FCSTD DOCUMENT  (FreeCAD 0.19R24291 (Git))
Label: test
License: All rights reserved
LicenseURL: http://en.wikipedia.org/wiki/All_rights_reserved
objects: Part::Part2DObjectPython×59
note: 59 computed .brp shape members not serialized (recipe doc carries the construction recipe); baked Part::Feature solids carry a one-line shape summary decoded from their .brp

FEATURE [Part::Part2DObjectPython] Line  # Draft 2D object (typed FeaturePython)
  Area = 0
  ChamferSize = 0
  Closed = false
  End = (-1266.79,1133.62,0)
  FilletRadius = 0
  Length = 3029.77
  MakeFace = true
  Points = (2) [(-901.491,-1874.05,0),(-1266.79,1133.62,0)]
  Start = (-901.491,-1874.05,0)
  Subdivisions = 0
  type = Beam
FEATURE [Part::Part2DObjectPython] Line001  # Draft 2D object (typed FeaturePython)
  Area = 0
  ChamferSize = 0
  Closed = false
  End = (-719.583,3387.59,0)
  FilletRadius = 0
  Length = 2319.45
  MakeFace = true
  Points = (2) [(-1266.79,1133.62,0),(-719.583,3387.59,0)]
  Start = (-1266.79,1133.62,0)
  Subdivisions = 0
  type = Beam
FEATURE [Part::Part2DObjectPython] Line002  # Draft 2D object (typed FeaturePython)
  Area = 0
  ChamferSize = 0
  Closed = false
  End = (-585.639,4946.22,0)
  FilletRadius = 0
  Length = 1564.37
  MakeFace = true
  Points = (2) [(-719.583,3387.59,0),(-585.639,4946.22,0)]
  Start = (-719.583,3387.59,0)
  Subdivisions = 0
  type = Beam
FEATURE [Part::Part2DObjectPython] Line003  # Draft 2D object (typed FeaturePython)
  Area = 0
  ChamferSize = 0
  Closed = false
  End = (-208.337,6520.16,0)
  FilletRadius = 0
  Length = 1618.53
  MakeFace = true
  Points = (2) [(-585.639,4946.22,0),(-208.337,6520.16,0)]
  Start = (-585.639,4946.22,0)
  Subdivisions = 0
  type = Beam
FEATURE [Part::Part2DObjectPython] Line004  # Draft 2D object (typed FeaturePython)
  Area = 0
  ChamferSize = 0
  Closed = false
  End = (510.393,7946.01,0)
  FilletRadius = 0
  Length = 1596.75
  MakeFace = true
  Points = (2) [(-208.337,6520.16,0),(510.393,7946.01,0)]
  Start = (-208.337,6520.16,0)
  Subdivisions = 0
  type = Beam
FEATURE [Part::Part2DObjectPython] Line005  # Draft 2D object (typed FeaturePython)
  Area = 0
  ChamferSize = 0
  Closed = false
  End = (486.04,9054.09,0)
  FilletRadius = 0
  Length = 1108.35
  MakeFace = true
  Points = (2) [(510.393,7946.01,0),(486.04,9054.09,0)]
  Start = (510.393,7946.01,0)
  Subdivisions = 0
  type = Beam
FEATURE [Part::Part2DObjectPython] Line006  # Draft 2D object (typed FeaturePython)
  Area = 0
  ChamferSize = 0
  Closed = false
  End = (120.663,10554.8,0)
  FilletRadius = 0
  Length = 1544.54
  MakeFace = true
  Points = (2) [(486.04,9054.09,0),(120.663,10554.8,0)]
  Start = (486.04,9054.09,0)
  Subdivisions = 0
  type = Beam
FEATURE [Part::Part2DObjectPython] Line007  # Draft 2D object (typed FeaturePython)
  Area = 0
  ChamferSize = 0
  Closed = false
  End = (-2616.71,977.139,0)
  FilletRadius = 0
  Length = 2215.24
  MakeFace = true
  Points = (2) [(-4757.6,408.041,0),(-2616.71,977.139,0)]
  Start = (-4757.6,408.041,0)
  Subdivisions = 0
  type = Beam
FEATURE [Part::Part2DObjectPython] Line008  # Draft 2D object (typed FeaturePython)
  Area = 0
  ChamferSize = 0
  Closed = false
  End = (-1912.11,841.639,0)
  FilletRadius = 0
  Length = 717.507
  MakeFace = true
  Points = (2) [(-2616.71,977.139,0),(-1912.11,841.639,0)]
  Start = (-2616.71,977.139,0)
  Subdivisions = 0
  type = Beam
FEATURE [Part::Part2DObjectPython] Line009  # Draft 2D object (typed FeaturePython)
  Area = 0
  ChamferSize = 0
  Closed = false
  End = (-1266.79,1133.62,0)
  FilletRadius = 0
  Length = 708.299
  MakeFace = true
  Points = (2) [(-1912.11,841.639,0),(-1266.79,1133.62,0)]
  Start = (-1912.11,841.639,0)
  Subdivisions = 0
  type = Beam
FEATURE [Part::Part2DObjectPython] Line010  # Draft 2D object (typed FeaturePython)
  Area = 0
  ChamferSize = 0
  Closed = false
  End = (-150.615,977.139,0)
  FilletRadius = 0
  Length = 1127.09
  MakeFace = true
  Points = (2) [(-1266.79,1133.62,0),(-150.615,977.139,0)]
  Start = (-1266.79,1133.62,0)
  Subdivisions = 0
  type = Beam
FEATURE [Part::Part2DObjectPython] Line011  # Draft 2D object (typed FeaturePython)
  Area = 0
  ChamferSize = 0
  Closed = false
  End = (716.583,706.14,0)
  FilletRadius = 0
  Length = 908.555
  MakeFace = true
  Points = (2) [(-150.615,977.139,0),(716.583,706.14,0)]
  Start = (-150.615,977.139,0)
  Subdivisions = 0
  type = Beam
FEATURE [Part::Part2DObjectPython] Line012  # Draft 2D object (typed FeaturePython)
  Area = 0
  ChamferSize = 0
  Closed = false
  End = (1583.78,733.239,0)
  FilletRadius = 0
  Length = 867.621
  MakeFace = true
  Points = (2) [(716.583,706.14,0),(1583.78,733.239,0)]
  Start = (716.583,706.14,0)
  Subdivisions = 0
  type = Beam
FEATURE [Part::Part2DObjectPython] Line013  # Draft 2D object (typed FeaturePython)
  Area = 0
  ChamferSize = 0
  Closed = false
  End = (2559.38,977.139,0)
  FilletRadius = 0
  Length = 1005.62
  MakeFace = true
  Points = (2) [(1583.78,733.239,0),(2559.38,977.139,0)]
  Start = (1583.78,733.239,0)
  Subdivisions = 0
  type = Beam
FEATURE [Part::Part2DObjectPython] Line014  # Draft 2D object (typed FeaturePython)
  Area = 0
  ChamferSize = 0
  Closed = false
  End = (3372.38,1329.44,0)
  FilletRadius = 0
  Length = 886.048
  MakeFace = true
  Points = (2) [(2559.38,977.139,0),(3372.38,1329.44,0)]
  Start = (2559.38,977.139,0)
  Subdivisions = 0
  type = Beam
FEATURE [Part::Part2DObjectPython] Line015  # Draft 2D object (typed FeaturePython)
  Area = 0
  ChamferSize = 0
  Closed = false
  End = (4185.37,1546.24,0)
  FilletRadius = 0
  Length = 841.407
  MakeFace = true
  Points = (2) [(3372.38,1329.44,0),(4185.37,1546.24,0)]
  Start = (3372.38,1329.44,0)
  Subdivisions = 0
  type = Beam
FEATURE [Part::Part2DObjectPython] Line016  # Draft 2D object (typed FeaturePython)
  Area = 0
  ChamferSize = 0
  Closed = false
  End = (5079.67,1356.54,0)
  FilletRadius = 0
  Length = 914.196
  MakeFace = true
  Points = (2) [(4185.37,1546.24,0),(5079.67,1356.54,0)]
  Start = (4185.37,1546.24,0)
  Subdivisions = 0
  type = Beam
FEATURE [Part::Part2DObjectPython] Line017  # Draft 2D object (typed FeaturePython)
  Area = 0
  ChamferSize = 0
  Closed = false
  End = (-1017.81,9351.02,0)
  FilletRadius = 0
  Length = 1656.87
  MakeFace = true
  Points = (2) [(120.663,10554.8,0),(-1017.81,9351.02,0)]
  Start = (120.663,10554.8,0)
  Subdivisions = 0
  type = Beam
FEATURE [Part::Part2DObjectPython] Line018  # Draft 2D object (typed FeaturePython)
  Area = 0
  ChamferSize = 0
  Closed = false
  End = (-2481.21,8971.62,0)
  FilletRadius = 0
  Length = 1511.78
  MakeFace = true
  Points = (2) [(-1017.81,9351.02,0),(-2481.21,8971.62,0)]
  Start = (-1017.81,9351.02,0)
  Subdivisions = 0
  type = Beam
FEATURE [Part::Part2DObjectPython] Line019  # Draft 2D object (typed FeaturePython)
  Area = 0
  ChamferSize = 0
  Closed = false
  End = (-3656.96,8788.47,0)
  FilletRadius = 0
  Length = 1189.93
  MakeFace = true
  Points = (2) [(-2481.21,8971.62,0),(-3656.96,8788.47,0)]
  Start = (-2481.21,8971.62,0)
  Subdivisions = 0
  type = Beam
FEATURE [Part::Part2DObjectPython] Line020  # Draft 2D object (typed FeaturePython)
  Area = 0
  ChamferSize = 0
  Closed = false
  End = (-4567.9,8131.52,0)
  FilletRadius = 0
  Length = 1123.12
  MakeFace = true
  Points = (2) [(-3656.96,8788.47,0),(-4567.9,8131.52,0)]
  Start = (-3656.96,8788.47,0)
  Subdivisions = 0
  type = Beam
FEATURE [Part::Part2DObjectPython] Line021  # Draft 2D object (typed FeaturePython)
  Area = 0
  ChamferSize = 0
  Closed = false
  End = (-5868.7,7101.72,0)
  FilletRadius = 0
  Length = 1659.08
  MakeFace = true
  Points = (2) [(-4567.9,8131.52,0),(-5868.7,7101.72,0)]
  Start = (-4567.9,8131.52,0)
  Subdivisions = 0
  type = Beam
FEATURE [Part::Part2DObjectPython] Line022  # Draft 2D object (typed FeaturePython)
  Area = 0
  ChamferSize = 0
  Closed = false
  End = (-6112.6,5936.43,0)
  FilletRadius = 0
  Length = 1190.55
  MakeFace = true
  Points = (2) [(-5868.7,7101.72,0),(-6112.6,5936.43,0)]
  Start = (-5868.7,7101.72,0)
  Subdivisions = 0
  type = Beam
FEATURE [Part::Part2DObjectPython] Line023  # Draft 2D object (typed FeaturePython)
  Area = 0
  ChamferSize = 0
  Closed = false
  End = (-6790.1,4852.43,0)
  FilletRadius = 0
  Length = 1278.3
  MakeFace = true
  Points = (2) [(-6112.6,5936.43,0),(-6790.1,4852.43,0)]
  Start = (-6112.6,5936.43,0)
  Subdivisions = 0
  type = Beam
FEATURE [Part::Part2DObjectPython] Line024  # Draft 2D object (typed FeaturePython)
  Area = 0
  ChamferSize = 0
  Closed = false
  End = (-6817.2,3903.93,0)
  FilletRadius = 0
  Length = 948.886
  MakeFace = true
  Points = (2) [(-6790.1,4852.43,0),(-6817.2,3903.93,0)]
  Start = (-6790.1,4852.43,0)
  Subdivisions = 0
  type = Beam
FEATURE [Part::Part2DObjectPython] Line025  # Draft 2D object (typed FeaturePython)
  Area = 0
  ChamferSize = 0
  Closed = false
  End = (-6519.1,2955.43,0)
  FilletRadius = 0
  Length = 994.239
  MakeFace = true
  Points = (2) [(-6817.2,3903.93,0),(-6519.1,2955.43,0)]
  Start = (-6817.2,3903.93,0)
  Subdivisions = 0
  type = Beam
FEATURE [Part::Part2DObjectPython] Line026  # Draft 2D object (typed FeaturePython)
  Area = 0
  ChamferSize = 0
  Closed = false
  End = (-5977.1,1871.44,0)
  FilletRadius = 0
  Length = 1211.95
  MakeFace = true
  Points = (2) [(-6519.1,2955.43,0),(-5977.1,1871.44,0)]
  Start = (-6519.1,2955.43,0)
  Subdivisions = 0
  type = Beam
FEATURE [Part::Part2DObjectPython] Line027  # Draft 2D object (typed FeaturePython)
  Area = 0
  ChamferSize = 0
  Closed = false
  End = (-4757.6,408.041,0)
  FilletRadius = 0
  Length = 1904.91
  MakeFace = true
  Points = (2) [(-5977.1,1871.44,0),(-4757.6,408.041,0)]
  Start = (-5977.1,1871.44,0)
  Subdivisions = 0
  type = Beam
FEATURE [Part::Part2DObjectPython] Line028  # Draft 2D object (typed FeaturePython)
  Area = 0
  ChamferSize = 0
  Closed = false
  End = (1126.94,11916.2,0)
  FilletRadius = 0
  Length = 1692.96
  MakeFace = true
  Points = (2) [(120.663,10554.8,0),(1126.94,11916.2,0)]
  Start = (120.663,10554.8,0)
  Subdivisions = 0
  type = Beam
FEATURE [Part::Part2DObjectPython] Line029  # Draft 2D object (typed FeaturePython)
  Area = 0
  ChamferSize = 0
  Closed = false
  End = (2347.26,12515.3,0)
  FilletRadius = 0
  Length = 1359.43
  MakeFace = true
  Points = (2) [(1126.94,11916.2,0),(2347.26,12515.3,0)]
  Start = (1126.94,11916.2,0)
  Subdivisions = 0
  type = Beam
FEATURE [Part::Part2DObjectPython] Line030  # Draft 2D object (typed FeaturePython)
  Area = 0
  ChamferSize = 0
  Closed = false
  End = (3745.07,12914.7,0)
  FilletRadius = 0
  Length = 1453.75
  MakeFace = true
  Points = (2) [(2347.26,12515.3,0),(3745.07,12914.7,0)]
  Start = (2347.26,12515.3,0)
  Subdivisions = 0
  type = Beam
FEATURE [Part::Part2DObjectPython] Line031  # Draft 2D object (typed FeaturePython)
  Area = 0
  ChamferSize = 0
  Closed = false
  End = (5231.64,12892.5,0)
  FilletRadius = 0
  Length = 1486.73
  MakeFace = true
  Points = (2) [(3745.07,12914.7,0),(5231.64,12892.5,0)]
  Start = (3745.07,12914.7,0)
  Subdivisions = 0
  type = Beam
FEATURE [Part::Part2DObjectPython] Line032  # Draft 2D object (typed FeaturePython)
  Area = 0
  ChamferSize = 0
  Closed = false
  End = (6474.14,12404.4,0)
  FilletRadius = 0
  Length = 1334.95
  MakeFace = true
  Points = (2) [(5231.64,12892.5,0),(6474.14,12404.4,0)]
  Start = (5231.64,12892.5,0)
  Subdivisions = 0
  type = Beam
FEATURE [Part::Part2DObjectPython] Line033  # Draft 2D object (typed FeaturePython)
  Area = 0
  ChamferSize = 0
  Closed = false
  End = (7295.08,11716.5,0)
  FilletRadius = 0
  Length = 1070.99
  MakeFace = true
  Points = (2) [(6474.14,12404.4,0),(7295.08,11716.5,0)]
  Start = (6474.14,12404.4,0)
  Subdivisions = 0
  type = Beam
FEATURE [Part::Part2DObjectPython] Line034  # Draft 2D object (typed FeaturePython)
  Area = 0
  ChamferSize = 0
  Closed = false
  End = (7827.58,10695.9,0)
  FilletRadius = 0
  Length = 1151.19
  MakeFace = true
  Points = (2) [(7295.08,11716.5,0),(7827.58,10695.9,0)]
  Start = (7295.08,11716.5,0)
  Subdivisions = 0
  type = Beam
FEATURE [Part::Part2DObjectPython] Line035  # Draft 2D object (typed FeaturePython)
  Area = 0
  ChamferSize = 0
  Closed = false
  End = (8027.27,9630.91,0)
  FilletRadius = 0
  Length = 1083.56
  MakeFace = true
  Points = (2) [(7827.58,10695.9,0),(8027.27,9630.91,0)]
  Start = (7827.58,10695.9,0)
  Subdivisions = 0
  type = Beam
FEATURE [Part::Part2DObjectPython] Line036  # Draft 2D object (typed FeaturePython)
  Area = 0
  ChamferSize = 0
  Closed = false
  End = (7938.52,8277.47,0)
  FilletRadius = 0
  Length = 1356.35
  MakeFace = true
  Points = (2) [(8027.27,9630.91,0),(7938.52,8277.47,0)]
  Start = (8027.27,9630.91,0)
  Subdivisions = 0
  type = Beam
FEATURE [Part::Part2DObjectPython] Line037  # Draft 2D object (typed FeaturePython)
  Area = 0
  ChamferSize = 0
  Closed = false
  End = (7716.65,7034.97,0)
  FilletRadius = 0
  Length = 1262.16
  MakeFace = true
  Points = (2) [(7938.52,8277.47,0),(7716.65,7034.97,0)]
  Start = (7938.52,8277.47,0)
  Subdivisions = 0
  type = Beam
FEATURE [Part::Part2DObjectPython] Line038  # Draft 2D object (typed FeaturePython)
  Area = 0
  ChamferSize = 0
  Closed = false
  End = (7295.08,5969.97,0)
  FilletRadius = 0
  Length = 1145.4
  MakeFace = true
  Points = (2) [(7716.65,7034.97,0),(7295.08,5969.97,0)]
  Start = (7716.65,7034.97,0)
  Subdivisions = 0
  type = Beam
FEATURE [Part::Part2DObjectPython] Line039  # Draft 2D object (typed FeaturePython)
  Area = 0
  ChamferSize = 0
  Closed = false
  End = (6585.08,4971.53,0)
  FilletRadius = 0
  Length = 1225.15
  MakeFace = true
  Points = (2) [(7295.08,5969.97,0),(6585.08,4971.53,0)]
  Start = (7295.08,5969.97,0)
  Subdivisions = 0
  type = Beam
FEATURE [Part::Part2DObjectPython] Line040  # Draft 2D object (typed FeaturePython)
  Area = 0
  ChamferSize = 0
  Closed = false
  End = (5586.64,3973.09,0)
  FilletRadius = 0
  Length = 1412.01
  MakeFace = true
  Points = (2) [(6585.08,4971.53,0),(5586.64,3973.09,0)]
  Start = (6585.08,4971.53,0)
  Subdivisions = 0
  type = Beam
FEATURE [Part::Part2DObjectPython] Line041  # Draft 2D object (typed FeaturePython)
  Area = 0
  ChamferSize = 0
  Closed = false
  End = (4122.26,3507.15,0)
  FilletRadius = 0
  Length = 1536.72
  MakeFace = true
  Points = (2) [(5586.64,3973.09,0),(4122.26,3507.15,0)]
  Start = (5586.64,3973.09,0)
  Subdivisions = 0
  type = Beam
FEATURE [Part::Part2DObjectPython] Line042  # Draft 2D object (typed FeaturePython)
  Area = 0
  ChamferSize = 0
  Closed = false
  End = (3412.26,2952.46,0)
  FilletRadius = 0
  Length = 900.99
  MakeFace = true
  Points = (2) [(4122.26,3507.15,0),(3412.26,2952.46,0)]
  Start = (4122.26,3507.15,0)
  Subdivisions = 0
  type = Beam
FEATURE [Part::Part2DObjectPython] Line043  # Draft 2D object (typed FeaturePython)
  Area = 0
  ChamferSize = 0
  Closed = false
  End = (2968.51,2198.08,0)
  FilletRadius = 0
  Length = 875.214
  MakeFace = true
  Points = (2) [(3412.26,2952.46,0),(2968.51,2198.08,0)]
  Start = (3412.26,2952.46,0)
  Subdivisions = 0
  type = Beam
FEATURE [Part::Part2DObjectPython] Line044  # Draft 2D object (typed FeaturePython)
  Area = 0
  ChamferSize = 0
  Closed = false
  End = (2965.88,1153.29,0)
  FilletRadius = 0
  Length = 1044.8
  MakeFace = true
  Points = (2) [(2968.51,2198.08,0),(2965.88,1153.29,0)]
  Start = (2968.51,2198.08,0)
  Subdivisions = 0
  type = Beam
FEATURE [Part::Part2DObjectPython] Line045  # Draft 2D object (typed FeaturePython)
  Area = 0
  ChamferSize = 0
  Closed = false
  End = (3264.5,45.5888,0)
  FilletRadius = 0
  Length = 1147.25
  MakeFace = true
  Points = (2) [(2965.88,1153.29,0),(3264.5,45.5888,0)]
  Start = (2965.88,1153.29,0)
  Subdivisions = 0
  type = Beam
FEATURE [Part::Part2DObjectPython] Line046  # Draft 2D object (typed FeaturePython)
  Area = 0
  ChamferSize = 0
  Closed = false
  End = (3785.05,-772.413,0)
  FilletRadius = 0
  Length = 969.586
  MakeFace = true
  Points = (2) [(3264.5,45.5888,0),(3785.05,-772.413,0)]
  Start = (3264.5,45.5888,0)
  Subdivisions = 0
  type = Beam
FEATURE [Part::Part2DObjectPython] Line047  # Draft 2D object (typed FeaturePython)
  Area = 0
  ChamferSize = 0
  Closed = false
  End = (2858.63,23.1706,0)
  FilletRadius = 0
  Length = 1135.2
  MakeFace = true
  Points = (2) [(2965.88,1153.29,0),(2858.63,23.1706,0)]
  Start = (2965.88,1153.29,0)
  Subdivisions = 0
  type = Beam
FEATURE [Part::Part2DObjectPython] Line048  # Draft 2D object (typed FeaturePython)
  Area = 0
  ChamferSize = 0
  Closed = false
  End = (2581.02,-892.662,0)
  FilletRadius = 0
  Length = 956.985
  MakeFace = true
  Points = (2) [(2858.63,23.1706,0),(2581.02,-892.662,0)]
  Start = (2858.63,23.1706,0)
  Subdivisions = 0
  type = Beam
FEATURE [Part::Part2DObjectPython] Line049  # Draft 2D object (typed FeaturePython)
  Area = 0
  ChamferSize = 0
  Closed = false
  End = (2360.63,-1341.59,0)
  FilletRadius = 0
  Length = 500.106
  MakeFace = true
  Points = (2) [(2581.02,-892.662,0),(2360.63,-1341.59,0)]
  Start = (2581.02,-892.662,0)
  Subdivisions = 0
  type = Beam
FEATURE [Part::Part2DObjectPython] Line050  # Draft 2D object (typed FeaturePython)
  Area = 0
  ChamferSize = 0
  Closed = false
  End = (2549.53,1644.51,0)
  FilletRadius = 0
  Length = 643.924
  MakeFace = true
  Points = (2) [(2965.88,1153.29,0),(2549.53,1644.51,0)]
  Start = (2965.88,1153.29,0)
  Subdivisions = 0
  type = Beam
FEATURE [Part::Part2DObjectPython] Line051  # Draft 2D object (typed FeaturePython)
  Area = 0
  ChamferSize = 0
  Closed = false
  End = (2252.07,2373.27,0)
  FilletRadius = 0
  Length = 787.133
  MakeFace = true
  Points = (2) [(2549.53,1644.51,0),(2252.07,2373.27,0)]
  Start = (2549.53,1644.51,0)
  Subdivisions = 0
  type = Beam
FEATURE [Part::Part2DObjectPython] Line052  # Draft 2D object (typed FeaturePython)
  Area = 0
  ChamferSize = 0
  Closed = false
  End = (2162.84,3295.38,0)
  FilletRadius = 0
  Length = 926.419
  MakeFace = true
  Points = (2) [(2252.07,2373.27,0),(2162.84,3295.38,0)]
  Start = (2252.07,2373.27,0)
  Subdivisions = 0
  type = Beam
FEATURE [Part::Part2DObjectPython] Line053  # Draft 2D object (typed FeaturePython)
  Area = 0
  ChamferSize = 0
  Closed = false
  End = (2326.44,4336.47,0)
  FilletRadius = 0
  Length = 1053.87
  MakeFace = true
  Points = (2) [(2162.84,3295.38,0),(2326.44,4336.47,0)]
  Start = (2162.84,3295.38,0)
  Subdivisions = 0
  type = Beam
FEATURE [Part::Part2DObjectPython] Line054  # Draft 2D object (typed FeaturePython)
  Area = 0
  ChamferSize = 0
  Closed = false
  End = (2475.17,4990.88,0)
  FilletRadius = 0
  Length = 671.089
  MakeFace = true
  Points = (2) [(2326.44,4336.47,0),(2475.17,4990.88,0)]
  Start = (2326.44,4336.47,0)
  Subdivisions = 0
  type = Beam
FEATURE [Part::Part2DObjectPython] Line055  # Draft 2D object (typed FeaturePython)
  Area = 0
  ChamferSize = 0
  Closed = false
  End = (2965.88,1153.29,0)
  FilletRadius = 0
  Length = 2478.06
  MakeFace = true
  Points = (2) [(1434.07,-794.627,0),(2965.88,1153.29,0)]
  Start = (1434.07,-794.627,0)
  Subdivisions = 0
  type = Beam
FEATURE [Part::Part2DObjectPython] Line056  # Draft 2D object (typed FeaturePython)
  Area = 0
  ChamferSize = 0
  Closed = false
  End = (3873.21,2239.42,0)
  FilletRadius = 0
  Length = 1415.24
  MakeFace = true
  Points = (2) [(2965.88,1153.29,0),(3873.21,2239.42,0)]
  Start = (2965.88,1153.29,0)
  Subdivisions = 0
  type = Beam
FEATURE [Part::Part2DObjectPython] Line057  # Draft 2D object (typed FeaturePython)
  Area = 0
  ChamferSize = 0
  Closed = false
  End = (4765.57,2685.6,0)
  FilletRadius = 0
  Length = 997.695
  MakeFace = true
  Points = (2) [(3873.21,2239.42,0),(4765.57,2685.6,0)]
  Start = (3873.21,2239.42,0)
  Subdivisions = 0
  type = Beam
FEATURE [Part::Part2DObjectPython] Line058  # Draft 2D object (typed FeaturePython)
  Area = 0
  ChamferSize = 0
  Closed = false
  End = (5955.39,3221.02,0)
  FilletRadius = 0
  Length = 1304.74
  MakeFace = true
  Points = (2) [(4765.57,2685.6,0),(5955.39,3221.02,0)]
  Start = (4765.57,2685.6,0)
  Subdivisions = 0
  type = Beam
